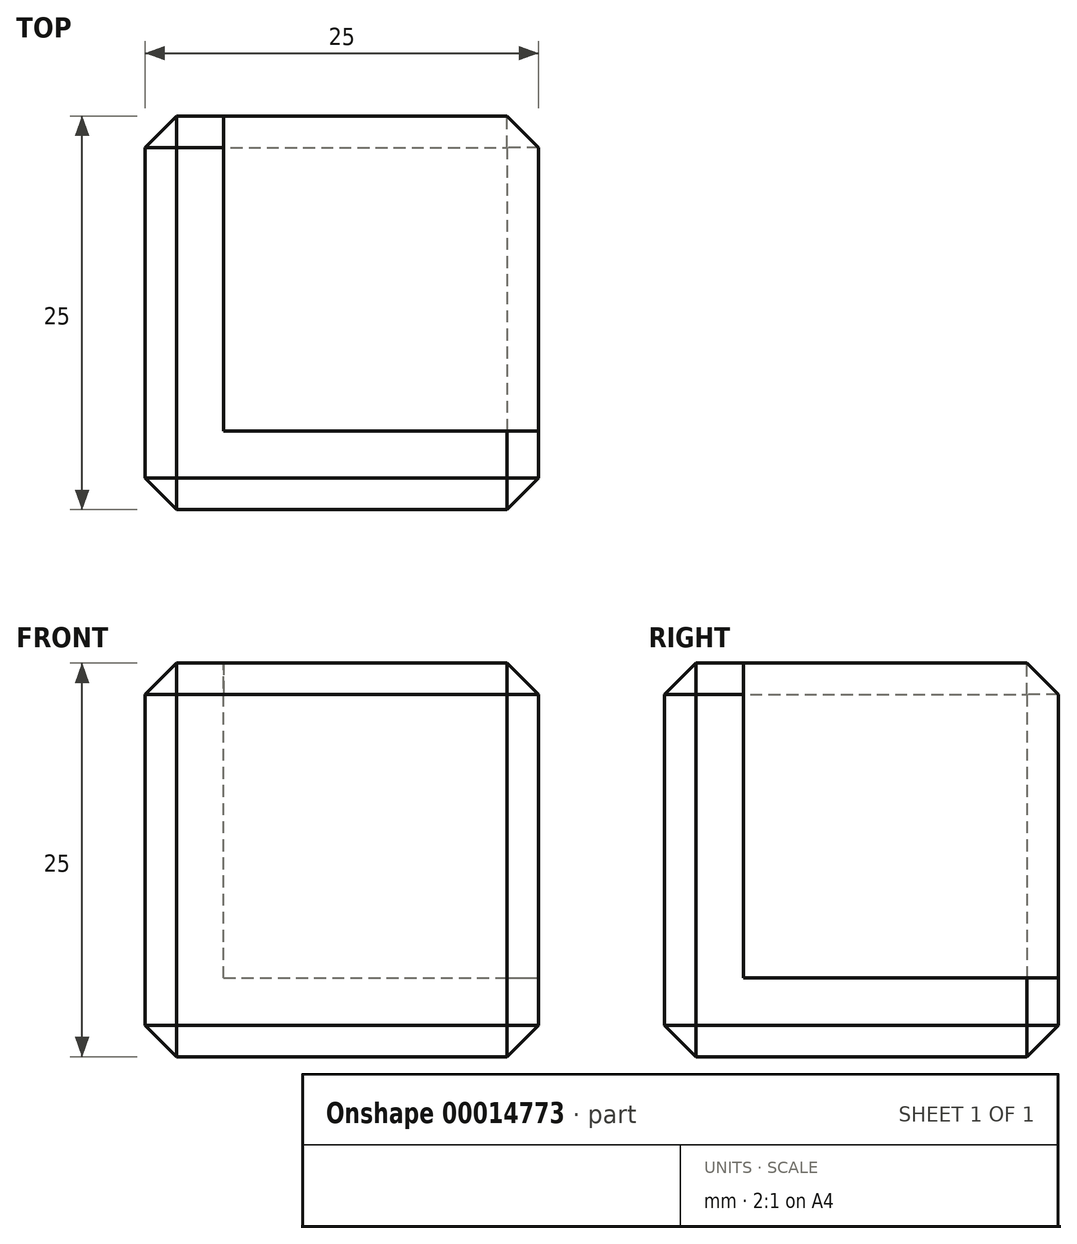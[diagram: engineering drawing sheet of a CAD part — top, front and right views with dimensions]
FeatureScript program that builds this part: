
annotation { "Feature Type Name" : "Feature", "Feature Type Description" : "" }
export const myFeature = defineFeature(function(context is Context, id is Id, definition is map)
    precondition{}
    {
        {
            var Q0;
            Q0=qCreatedBy(makeId("Top.planeOp"),FACE);
            var sketch = newSketch(context, id + "F0", { "sketchPlane" : qUnion([Q0])});
            skLineSegment(sketch, "E0.bottom", {"start": v(-12.87, 14.16) * mm, "end": v(12.13, 14.16) * mm});
            skLineSegment(sketch, "E0.top", {"start": v(-12.87, -10.84) * mm, "end": v(12.13, -10.84) * mm});
            skLineSegment(sketch, "E0.left", {"start": v(-12.87, 14.16) * mm, "end": v(-12.87, -10.84) * mm});
            skLineSegment(sketch, "E0.right", {"start": v(12.13, 14.16) * mm, "end": v(12.13, -10.84) * mm});
            skSolve(sketch);
        }
        {
            var Q0;
            Q0=makeQuery(id+"F0.imprint","IMPRINT",FACE,{"disambiguationData":[TD([[makeQuery(id+"F0.imprint","IMPRINT",EDGE,{"derivedFrom":sQuery(id+"F0.wireOp",EDGE,"E0.bottom")}),-1.0]])]});
            extrude(context, id + "F1", {"entities" : qUnion([Q0]), "depth" : 25 * mm});
        }
        {
            var Q0;
            Q0=makeQuery(id+"F1.opExtrude","CAP_FACE",FACE,{"disambiguationData":[OSD([sQuery(id+"F0.wireOp",EDGE,"E0.bottom"),sQuery(id+"F0.wireOp",EDGE,"E0.top"),sQuery(id+"F0.wireOp",EDGE,"E0.left"),sQuery(id+"F0.wireOp",EDGE,"E0.right")])],"isStart":false});
            var sketch = newSketch(context, id + "F2", { "sketchPlane" : qUnion([Q0])});
            skLineSegment(sketch, "E1", {"start": v(-7.87, 14.16) * mm, "end": v(-7.87, -5.84) * mm});
            skLineSegment(sketch, "E2", {"start": v(-7.87, -5.84) * mm, "end": v(12.13, -5.84) * mm});
            skLineSegment(sketch, "E3", {"start": v(12.13, -5.84) * mm, "end": v(12.13, 14.16) * mm});
            skLineSegment(sketch, "E4", {"start": v(12.13, 14.16) * mm, "end": v(-7.87, 14.16) * mm});
            skSolve(sketch);
        }
        {
            var Q0;
            Q0=makeQuery(id+"F2.imprint","IMPRINT",FACE,{"disambiguationData":[TD([[makeQuery(id+"F2.imprint","IMPRINT",EDGE,{"derivedFrom":sQuery(id+"F2.wireOp",EDGE,"E1")}),1.0]])]});
            extrude(context, id + "F3", {"entities" : qUnion([Q0]), "operationType" : NewBodyOperationType.REMOVE, "oppositeDirection" : true, "depth" : 20 * mm});
        }
        {
            var Q0;
            Q0=makeQuery(id+"F1.opExtrude","SWEPT_EDGE",EDGE,{"disambiguationData":[OSD([sQuery(id+"F0.wireOp",EDGE,"E0.top"),sQuery(id+"F0.wireOp",EDGE,"E0.left")])]});
            var Q1;
            Q1=makeQuery(id+"F1.opExtrude","CAP_EDGE",EDGE,{"disambiguationData":[OSD([sQuery(id+"F0.wireOp",EDGE,"E0.left")])],"isStart":false});
            var Q2;
            Q2=makeQuery(id+"F1.opExtrude","CAP_EDGE",EDGE,{"disambiguationData":[OSD([sQuery(id+"F0.wireOp",EDGE,"E0.top")])],"isStart":false});
            var Q3;
            Q3=makeQuery(id+"F1.opExtrude","SWEPT_EDGE",EDGE,{"disambiguationData":[OSD([sQuery(id+"F0.wireOp",EDGE,"E0.top"),sQuery(id+"F0.wireOp",EDGE,"E0.right")])]});
            var Q4;
            Q4=makeQuery(id+"F1.opExtrude","CAP_EDGE",EDGE,{"disambiguationData":[OSD([sQuery(id+"F0.wireOp",EDGE,"E0.top")])],"isStart":true});
            var Q5;
            Q5=makeQuery(id+"F1.opExtrude","CAP_EDGE",EDGE,{"disambiguationData":[OSD([sQuery(id+"F0.wireOp",EDGE,"E0.right")])],"isStart":true});
            var Q6;
            Q6=makeQuery(id+"F1.opExtrude","CAP_EDGE",EDGE,{"disambiguationData":[OSD([sQuery(id+"F0.wireOp",EDGE,"E0.bottom")])],"isStart":true});
            var Q7;
            Q7=makeQuery(id+"F1.opExtrude","SWEPT_EDGE",EDGE,{"disambiguationData":[OSD([sQuery(id+"F0.wireOp",EDGE,"E0.bottom"),sQuery(id+"F0.wireOp",EDGE,"E0.left")])]});
            var Q8;
            Q8=makeQuery(id+"F1.opExtrude","CAP_EDGE",EDGE,{"disambiguationData":[OSD([sQuery(id+"F0.wireOp",EDGE,"E0.left")])],"isStart":true});
            var Q9;
            Q9=makeQuery(id+"F1.opExtrude","CAP_EDGE",EDGE,{"disambiguationData":[OSD([sQuery(id+"F0.wireOp",EDGE,"E0.right")])],"isStart":false});
            var Q10;
            Q10=makeQuery(id+"F1.opExtrude","SWEPT_EDGE",EDGE,{"disambiguationData":[OSD([sQuery(id+"F0.wireOp",EDGE,"E0.bottom"),sQuery(id+"F0.wireOp",EDGE,"E0.right")])]});
            var Q11;
            Q11=makeQuery(id+"F1.opExtrude","CAP_EDGE",EDGE,{"disambiguationData":[OSD([sQuery(id+"F0.wireOp",EDGE,"E0.bottom")])],"isStart":false});
            chamfer(context, id + "F4", {"entities" : qUnion([Q0, Q1, Q2, Q3, Q4, Q5, Q6, Q7, Q8, Q9, Q10, Q11]), "width" : 2 * mm, "tangentPropagation" : true});
        }
    });
